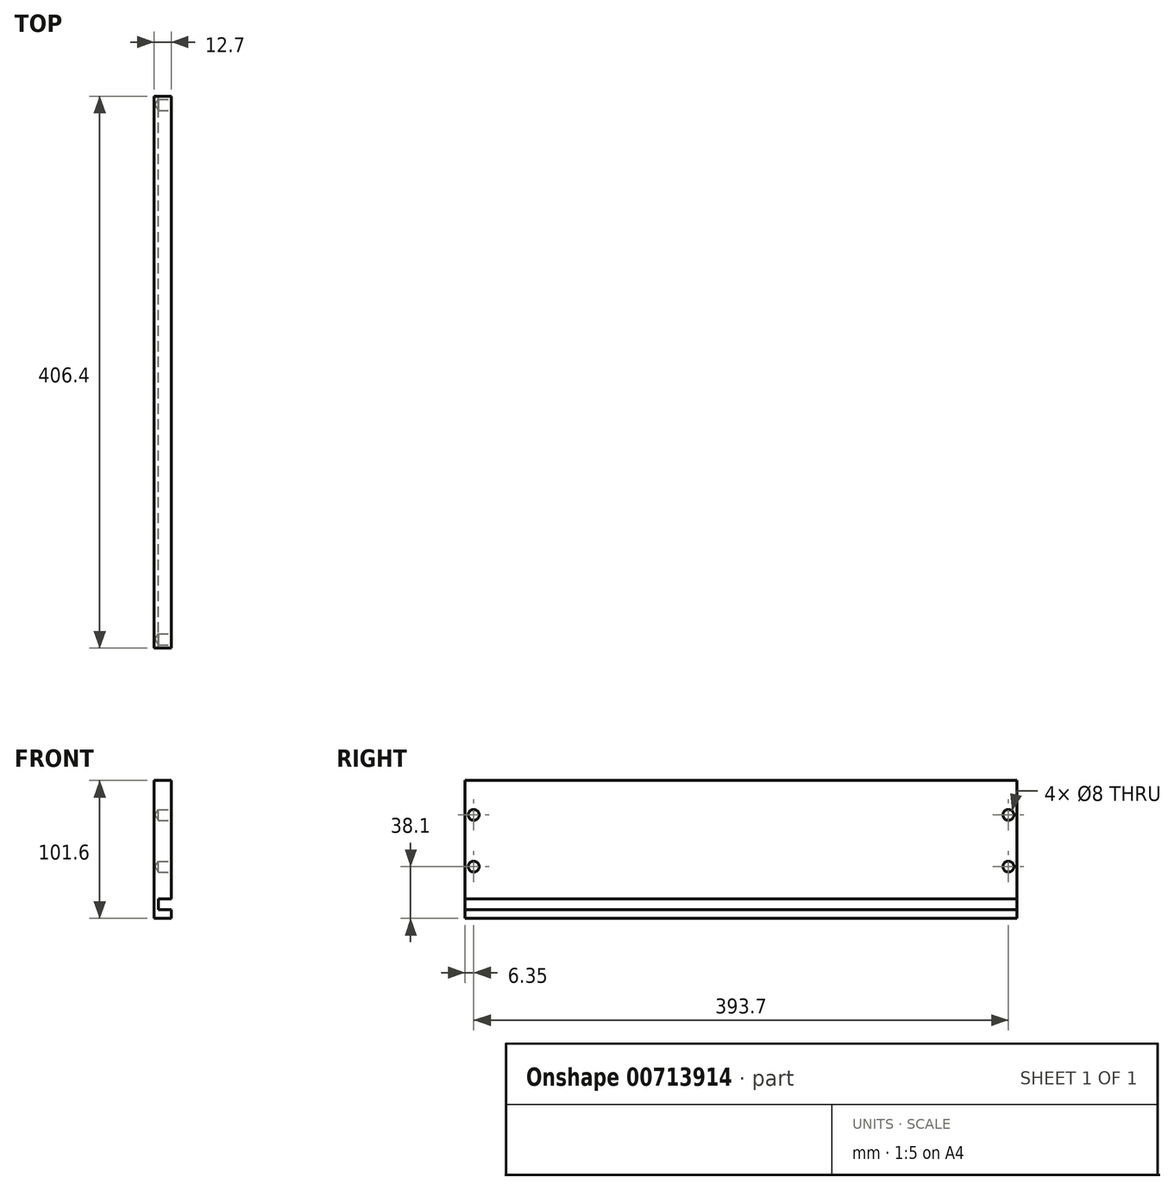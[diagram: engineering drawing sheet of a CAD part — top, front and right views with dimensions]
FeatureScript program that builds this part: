
annotation { "Feature Type Name" : "Feature", "Feature Type Description" : "" }
export const myFeature = defineFeature(function(context is Context, id is Id, definition is map)
    precondition{}
    {
        {
            var Q0;
            Q0=qCreatedBy(makeId("Right.planeOp"),FACE);
            var sketch = newSketch(context, id + "F0", { "sketchPlane" : qUnion([Q0])});
            skLineSegment(sketch, "E0.bottom", {"start": v(-203.2, 50.8) * mm, "end": v(203.2, 50.8) * mm});
            skLineSegment(sketch, "E0.top", {"start": v(-203.2, -50.8) * mm, "end": v(203.2, -50.8) * mm});
            skLineSegment(sketch, "E0.left", {"start": v(-203.2, 50.8) * mm, "end": v(-203.2, -50.8) * mm});
            skLineSegment(sketch, "E0.right", {"start": v(203.2, 50.8) * mm, "end": v(203.2, -50.8) * mm});
            skPoint(sketch, "E0.middle", {"position": v(0, 0) * mm});
            skSolve(sketch);
        }
        {
            var Q0;
            Q0=makeQuery(id+"F0.imprint","IMPRINT",FACE,{"disambiguationData":[TD([[makeQuery(id+"F0.imprint","IMPRINT",EDGE,{"derivedFrom":sQuery(id+"F0.wireOp",EDGE,"E0.bottom")}),-1.0]])]});
            extrude(context, id + "F1", {"entities" : qUnion([Q0]), "depth" : 12.7 * mm, "offsetDistance" : 25.4 * mm});
        }
        {
            var Q0;
            Q0=makeQuery(id+"F1.opExtrude","CAP_FACE",FACE,{"disambiguationData":[OSD([sQuery(id+"F0.wireOp",EDGE,"E0.bottom"),sQuery(id+"F0.wireOp",EDGE,"E0.top"),sQuery(id+"F0.wireOp",EDGE,"E0.left"),sQuery(id+"F0.wireOp",EDGE,"E0.right")])],"isStart":false});
            var sketch = newSketch(context, id + "F2", { "sketchPlane" : qUnion([Q0])});
            skLineSegment(sketch, "E1", {"start": v(-203.2, -50.8) * mm, "end": v(-203.2, -44.45) * mm});
            skLineSegment(sketch, "E2.bottom", {"start": v(-203.2, -44.45) * mm, "end": v(203.2, -44.45) * mm});
            skLineSegment(sketch, "E2.top", {"start": v(-203.2, -36.58) * mm, "end": v(203.2, -36.58) * mm});
            skLineSegment(sketch, "E2.left", {"start": v(-203.2, -44.45) * mm, "end": v(-203.2, -36.58) * mm});
            skLineSegment(sketch, "E2.right", {"start": v(203.2, -44.45) * mm, "end": v(203.2, -36.58) * mm});
            skSolve(sketch);
        }
        {
            var Q0;
            Q0=makeQuery(id+"F2.imprint","IMPRINT",FACE,{"disambiguationData":[TD([[makeQuery(id+"F2.imprint","IMPRINT",EDGE,{"derivedFrom":sQuery(id+"F2.wireOp",EDGE,"E2.bottom")}),1.0]])]});
            extrude(context, id + "F3", {"entities" : qUnion([Q0]), "operationType" : NewBodyOperationType.REMOVE, "oppositeDirection" : true, "depth" : 9.65 * mm, "offsetDistance" : 25.4 * mm});
        }
        {
            var Q0;
            {var subQ0=sQuery(id+"F0.wireOp",EDGE,"E0.bottom");var subQ1=sQuery(id+"F0.wireOp",EDGE,"E0.right");var subQ2=sQuery(id+"F0.wireOp",EDGE,"E0.left");Q0=makeQuery(id+"F3.boolean.opBoolean","SPLIT",FACE,{"disambiguationData":[TD([makeQuery(id+"F1.opExtrude","SWEPT_FACE",FACE,{"disambiguationData":[OSD([subQ0])]})])],"derivedFrom":makeQuery(id+"F1.opExtrude","CAP_FACE",FACE,{"disambiguationData":[OSD([subQ0,sQuery(id+"F0.wireOp",EDGE,"E0.top"),subQ2,subQ1])],"isStart":false})});}
            var sketch = newSketch(context, id + "F4", { "sketchPlane" : qUnion([Q0])});
            skLineSegment(sketch, "E3", {"start": v(-203.2, 50.8) * mm, "end": v(-196.85, 50.8) * mm});
            skLineSegment(sketch, "E4", {"start": v(-196.85, 50.8) * mm, "end": v(-196.85, 25.4) * mm});
            skLineSegment(sketch, "E5", {"start": v(-196.85, 25.4) * mm, "end": v(-196.85, -12.7) * mm});
            skLineSegment(sketch, "E6", {"start": v(203.2, 50.8) * mm, "end": v(196.85, 50.8) * mm});
            skLineSegment(sketch, "E7", {"start": v(196.85, 50.8) * mm, "end": v(196.85, 25.4) * mm});
            skLineSegment(sketch, "E8", {"start": v(196.85, 25.4) * mm, "end": v(196.85, -12.7) * mm});
            skSolve(sketch);
        }
        {
            var Q0;
            Q0=sQuery(id+"F4.wireOp",VERTEX,"E4.end");
            var Q1;
            Q1=sQuery(id+"F4.wireOp",VERTEX,"E5.end");
            var Q2;
            Q2=sQuery(id+"F4.wireOp",VERTEX,"E8.start");
            var Q3;
            Q3=sQuery(id+"F4.wireOp",VERTEX,"E8.end");
            var Q4;
            Q4=makeQuery(id+"F1.opExtrude","SWEPT_BODY",BODY,{"disambiguationData":[OSD([sQuery(id+"F0.wireOp",EDGE,"E0.bottom"),sQuery(id+"F0.wireOp",EDGE,"E0.top"),sQuery(id+"F0.wireOp",EDGE,"E0.left"),sQuery(id+"F0.wireOp",EDGE,"E0.right")])]});
            hole(context, id + "F5", {"style" : HoleStyle.SIMPLE, "endStyle" : HoleEndStyle.BLIND, "holeDiameter" : 8 * mm, "majorDiameter" : 6.35 * mm, "holeDepth" : 9.65 * mm, "isTappedThrough" : true, "tappedDepth" : 12.7 * mm, "tapClearance" : 3, "startFromSketch" : true, "locations" : qUnion([Q0, Q1, Q2, Q3]), "scope" : qUnion([Q4])});
        }
    });
